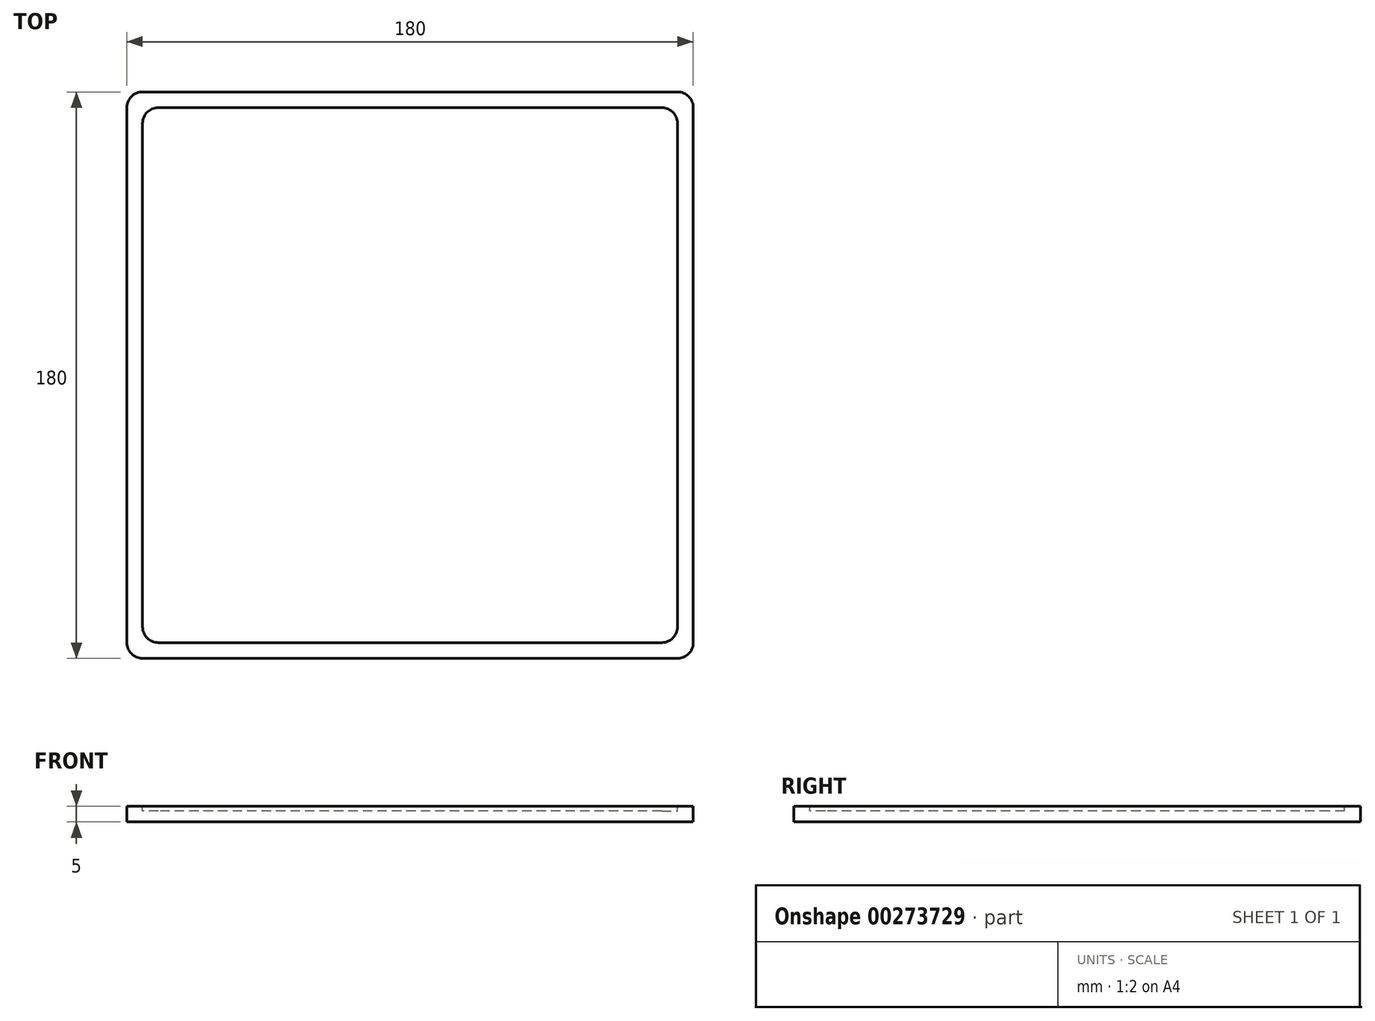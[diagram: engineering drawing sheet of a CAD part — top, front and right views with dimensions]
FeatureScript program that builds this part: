
annotation { "Feature Type Name" : "Feature", "Feature Type Description" : "" }
export const myFeature = defineFeature(function(context is Context, id is Id, definition is map)
    precondition{}
    {
        {
            var Q0;
            Q0=qCreatedBy(makeId("Top.planeOp"),FACE);
            var sketch = newSketch(context, id + "F0", { "sketchPlane" : qUnion([Q0])});
            skLineSegment(sketch, "E0.bottom", {"start": v(0, 180) * mm, "end": v(180, 180) * mm});
            skLineSegment(sketch, "E0.top", {"start": v(0, 0) * mm, "end": v(180, 0) * mm});
            skLineSegment(sketch, "E0.left", {"start": v(0, 180) * mm, "end": v(0, 0) * mm});
            skLineSegment(sketch, "E0.right", {"start": v(180, 180) * mm, "end": v(180, 0) * mm});
            skSolve(sketch);
        }
        {
            var Q0;
            Q0=makeQuery(id+"F0.imprint","IMPRINT",FACE,{"disambiguationData":[TD([[makeQuery(id+"F0.imprint","IMPRINT",EDGE,{"derivedFrom":sQuery(id+"F0.wireOp",EDGE,"E0.bottom")}),-1.0]])]});
            extrude(context, id + "F1", {"entities" : qUnion([Q0]), "depth" : 5 * mm});
        }
        {
            var Q0;
            Q0=makeQuery(id+"F1.opExtrude","CAP_FACE",FACE,{"disambiguationData":[OSD([sQuery(id+"F0.wireOp",EDGE,"E0.bottom"),sQuery(id+"F0.wireOp",EDGE,"E0.top"),sQuery(id+"F0.wireOp",EDGE,"E0.left"),sQuery(id+"F0.wireOp",EDGE,"E0.right")])],"isStart":false});
            var sketch = newSketch(context, id + "F2", { "sketchPlane" : qUnion([Q0])});
            skLineSegment(sketch, "E1.0", {"start": v(5, 175) * mm, "end": v(5, 5) * mm});
            skLineSegment(sketch, "E1.1", {"start": v(175, 175) * mm, "end": v(5, 175) * mm});
            skLineSegment(sketch, "E1.2", {"start": v(175, 5) * mm, "end": v(175, 175) * mm});
            skLineSegment(sketch, "E1.3", {"start": v(5, 5) * mm, "end": v(175, 5) * mm});
            skSolve(sketch);
        }
        {
            var Q0;
            Q0=makeQuery(id+"F2.imprint","IMPRINT",FACE,{"disambiguationData":[TD([[makeQuery(id+"F2.imprint","IMPRINT",EDGE,{"derivedFrom":sQuery(id+"F2.wireOp",EDGE,"E1.0")}),1.0]])]});
            extrude(context, id + "F3", {"entities" : qUnion([Q0]), "operationType" : NewBodyOperationType.REMOVE, "oppositeDirection" : true, "depth" : 1.5 * mm});
        }
        {
            var Q0;
            Q0=makeQuery(id+"F1.opExtrude","SWEPT_EDGE",EDGE,{"disambiguationData":[OSD([sQuery(id+"F0.wireOp",EDGE,"E0.bottom"),sQuery(id+"F0.wireOp",EDGE,"E0.left")])]});
            var Q1;
            Q1=makeQuery(id+"F1.opExtrude","SWEPT_EDGE",EDGE,{"disambiguationData":[OSD([sQuery(id+"F0.wireOp",EDGE,"E0.bottom"),sQuery(id+"F0.wireOp",EDGE,"E0.right")])]});
            var Q2;
            Q2=makeQuery(id+"F1.opExtrude","SWEPT_EDGE",EDGE,{"disambiguationData":[OSD([sQuery(id+"F0.wireOp",EDGE,"E0.top"),sQuery(id+"F0.wireOp",EDGE,"E0.right")])]});
            var Q3;
            Q3=makeQuery(id+"F1.opExtrude","SWEPT_EDGE",EDGE,{"disambiguationData":[OSD([sQuery(id+"F0.wireOp",EDGE,"E0.top"),sQuery(id+"F0.wireOp",EDGE,"E0.left")])]});
            var Q4;
            Q4=makeQuery(id+"F3.boolean.opBoolean","COPY",EDGE,{"derivedFrom":makeQuery(id+"F3.opExtrude","SWEPT_EDGE",EDGE,{"disambiguationData":[OSD([sQuery(id+"F2.wireOp",EDGE,"E1.2"),sQuery(id+"F2.wireOp",EDGE,"E1.3")])]})});
            var Q5;
            Q5=makeQuery(id+"F3.boolean.opBoolean","COPY",EDGE,{"derivedFrom":makeQuery(id+"F3.opExtrude","SWEPT_EDGE",EDGE,{"disambiguationData":[OSD([sQuery(id+"F2.wireOp",EDGE,"E1.1"),sQuery(id+"F2.wireOp",EDGE,"E1.2")])]})});
            var Q6;
            Q6=makeQuery(id+"F3.boolean.opBoolean","COPY",EDGE,{"derivedFrom":makeQuery(id+"F3.opExtrude","SWEPT_EDGE",EDGE,{"disambiguationData":[OSD([sQuery(id+"F2.wireOp",EDGE,"E1.0"),sQuery(id+"F2.wireOp",EDGE,"E1.3")])]})});
            var Q7;
            Q7=makeQuery(id+"F3.boolean.opBoolean","COPY",EDGE,{"derivedFrom":makeQuery(id+"F3.opExtrude","SWEPT_EDGE",EDGE,{"disambiguationData":[OSD([sQuery(id+"F2.wireOp",EDGE,"E1.0"),sQuery(id+"F2.wireOp",EDGE,"E1.1")])]})});
            fillet(context, id + "F4", {"entities" : qUnion([Q0, Q1, Q2, Q3, Q4, Q5, Q6, Q7]), "radius" : 5 * mm, "tangentPropagation" : true, "allowEdgeOverflow" : false});
        }
    });
